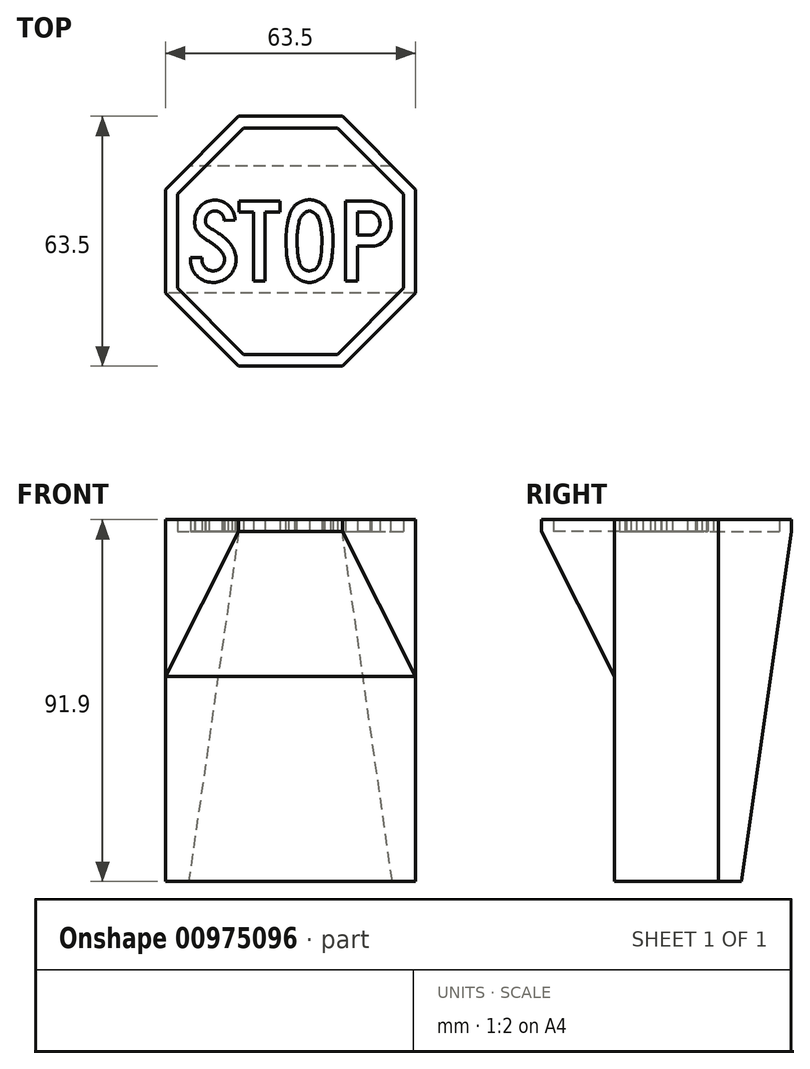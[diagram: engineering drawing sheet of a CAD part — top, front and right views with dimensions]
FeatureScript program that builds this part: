
annotation { "Feature Type Name" : "Feature", "Feature Type Description" : "" }
export const myFeature = defineFeature(function(context is Context, id is Id, definition is map)
    precondition{}
    {
        {
            var Q0;
            Q0=qCreatedBy(makeId("Top.planeOp"),FACE);
            var sketch = newSketch(context, id + "F0", { "sketchPlane" : qUnion([Q0])});
            skCircle(sketch, "E0.cCircle", {"center": v(0, 0) * mm, "radius": 34.37 * mm, "construction": true});
            skLineSegment(sketch, "E0.0", {"start": v(-13.15, 31.75) * mm, "end": v(13.15, 31.75) * mm});
            skLineSegment(sketch, "E0.1", {"start": v(13.15, 31.75) * mm, "end": v(31.75, 13.15) * mm});
            skLineSegment(sketch, "E0.2", {"start": v(31.75, 13.15) * mm, "end": v(31.75, -13.15) * mm});
            skLineSegment(sketch, "E0.3", {"start": v(31.75, -13.15) * mm, "end": v(13.15, -31.75) * mm});
            skLineSegment(sketch, "E0.4", {"start": v(13.15, -31.75) * mm, "end": v(-13.15, -31.75) * mm});
            skLineSegment(sketch, "E0.5", {"start": v(-13.15, -31.75) * mm, "end": v(-31.75, -13.15) * mm});
            skLineSegment(sketch, "E0.6", {"start": v(-31.75, -13.15) * mm, "end": v(-31.75, 13.15) * mm});
            skLineSegment(sketch, "E0.7", {"start": v(-31.75, 13.15) * mm, "end": v(-13.15, 31.75) * mm});
            skSolve(sketch);
        }
        {
            var Q0;
            Q0=qSketchRegion(id+"F0",true);
            extrude(context, id + "F1", {"entities" : qUnion([Q0]), "oppositeDirection" : true, "depth" : 88.9 * mm, "offsetDistance" : 25.4 * mm});
        }
        {
            var Q0;
            Q0=makeQuery(id+"F1.opExtrude","SWEPT_FACE",FACE,{"disambiguationData":[OSD([sQuery(id+"F0.wireOp",EDGE,"E0.6")])]});
            var sketch = newSketch(context, id + "F2", { "sketchPlane" : qUnion([Q0])});
            skLineSegment(sketch, "E1", {"start": v(0, 0) * mm, "end": v(-31.75, 0) * mm});
            skLineSegment(sketch, "E2.MirrorCS", {"start": v(0, 0) * mm, "end": v(31.75, 0) * mm});
            skLineSegment(sketch, "E3", {"start": v(31.75, 0) * mm, "end": v(31.75, -88.9) * mm});
            skLineSegment(sketch, "E4", {"start": v(14.66, -88.9) * mm, "end": v(-31.75, -88.9) * mm});
            skLineSegment(sketch, "E5", {"start": v(-31.75, -88.9) * mm, "end": v(-31.75, 0) * mm});
            skLineSegment(sketch, "E6", {"start": v(14.66, -88.9) * mm, "end": v(8.31, -88.9) * mm});
            skPoint(sketch, "E7.orphan", {"position": v(21.01, -88.9) * mm});
            skLineSegment(sketch, "E8", {"start": v(13.15, -88.9) * mm, "end": v(31.75, -88.9) * mm});
            skLineSegment(sketch, "E9", {"start": v(0, -88.9) * mm, "end": v(-6.35, -88.9) * mm});
            skLineSegment(sketch, "E10", {"start": v(-6.35, -88.9) * mm, "end": v(-12.7, -88.9) * mm});
            skLineSegment(sketch, "E11", {"start": v(-12.7, -88.9) * mm, "end": v(-19.05, -88.9) * mm});
            skLineSegment(sketch, "E12", {"start": v(-13.15, -88.9) * mm, "end": v(31.75, 0) * mm});
            skLineSegment(sketch, "E13", {"start": v(-19.05, -88.9) * mm, "end": v(-31.75, 0) * mm});
            skSolve(sketch);
        }
        {
            var Q0;
            {var subQ0=sQuery(id+"F2.wireOp",EDGE,"E5");Q0=makeQuery(id+"F2.imprint","IMPRINT",FACE,{"disambiguationData":[TD([[makeQuery(id+"F2.imprint","IMPRINT",EDGE,{"derivedFrom":subQ0}),-1.0]])]});}
            var Q1;
            {var subQ0=sQuery(id+"F2.wireOp",EDGE,"jV5SaWTU-9QsE-opv1-VP0P-y0ptpn6lwSnb");var subQ1=sQuery(id+"F0.wireOp",EDGE,"E0.6");var subQ2=makeQuery(id+"F1.opExtrude","SWEPT_EDGE",EDGE,{"disambiguationData":[OSD([sQuery(id+"F0.wireOp",EDGE,"E0.5"),subQ1])]});var subQ3=makeQuery(id+"F2.imprint","INTERSECT",VERTEX,{"derivedFrom":[subQ2,subQ0]});Q1=makeQuery(id+"F2.imprint","IMPRINT",FACE,{"disambiguationData":[TD([[makeQuery(id+"F2.imprint","IMPRINT",EDGE,{"disambiguationData":[TD([[subQ3,-1.0]])],"derivedFrom":subQ0}),1.0]])]});}
            var Q2;
            {var subQ0=sQuery(id+"F2.wireOp",EDGE,"E4");var subQ1=sQuery(id+"F2.wireOp",EDGE,"jV5SaWTU-9QsE-opv1-VP0P-y0ptpn6lwSnb");var subQ2=makeQuery(id+"F2.imprint","INTERSECT",VERTEX,{"derivedFrom":[sQuery(id+"F2.wireOp",EDGE,"heyR2Hmy-5QPG-FOdl-Z93e-mRFAagvmiP7r"),subQ1,subQ0]});Q2=makeQuery(id+"F2.imprint","IMPRINT",FACE,{"disambiguationData":[TD([[makeQuery(id+"F2.imprint","IMPRINT",EDGE,{"disambiguationData":[TD([[subQ2,-1.0]])],"derivedFrom":subQ1}),1.0]])]});}
            var Q3;
            {var subQ4=sQuery(id+"F2.wireOp",EDGE,"JUMX4e05-irpo-ZofT-aYDr-bJa91oU9Ee8P");var subQ6=sQuery(id+"F2.wireOp",EDGE,"AKcFHBRH-ovDV-q2iI-lgTK-DhJX03LWiosI");var subQ7=makeQuery(id+"F2.imprint","INTERSECT",VERTEX,{"derivedFrom":[subQ4,subQ6]});Q3=makeQuery(id+"F2.imprint","IMPRINT",FACE,{"disambiguationData":[TD([[makeQuery(id+"F2.imprint","IMPRINT",EDGE,{"disambiguationData":[TD([[subQ7,1.0]])],"derivedFrom":subQ4}),1.0]])]});}
            var Q4;
            {var subQ0=sQuery(id+"F2.wireOp",EDGE,"E4");var subQ1=makeQuery(id+"F1.opExtrude","SWEPT_EDGE",EDGE,{"disambiguationData":[OSD([sQuery(id+"F0.wireOp",EDGE,"E0.5"),sQuery(id+"F0.wireOp",EDGE,"E0.6")])]});var subQ2=makeQuery(id+"F2.imprint","INTERSECT",VERTEX,{"derivedFrom":[subQ1,subQ0]});Q4=makeQuery(id+"F2.imprint","IMPRINT",FACE,{"disambiguationData":[TD([[makeQuery(id+"F2.imprint","IMPRINT",EDGE,{"disambiguationData":[TD([[subQ2,1.0]])],"derivedFrom":subQ0}),-1.0]])]});}
            var Q5;
            Q5=makeQuery(id+"F1.opExtrude","SWEPT_FACE",FACE,{"disambiguationData":[OSD([sQuery(id+"F0.wireOp",EDGE,"E0.3")])]});
            var Q6;
            {var subQ0=sQuery(id+"F2.wireOp",EDGE,"E3");Q6=makeQuery(id+"F2.imprint","IMPRINT",FACE,{"disambiguationData":[TD([[makeQuery(id+"F2.imprint","IMPRINT",EDGE,{"derivedFrom":subQ0}),-1.0]])]});}
            var Q7;
            {var subQ0=sQuery(id+"F2.wireOp",EDGE,"VHKm9X3M-lhd3-aAJ8-6689-DRtZFMRUWEL7");var subQ1=sQuery(id+"F0.wireOp",EDGE,"E0.6");var subQ2=makeQuery(id+"F1.opExtrude","CAP_EDGE",EDGE,{"disambiguationData":[OSD([subQ1])],"isStart":false});var subQ3=makeQuery(id+"F2.imprint","INTERSECT",VERTEX,{"derivedFrom":[subQ2,sQuery(id+"F2.wireOp",EDGE,"E6"),subQ0]});Q7=makeQuery(id+"F2.imprint","IMPRINT",FACE,{"disambiguationData":[TD([[makeQuery(id+"F2.imprint","IMPRINT",EDGE,{"disambiguationData":[TD([[subQ3,-1.0]])],"derivedFrom":subQ0}),-1.0]])]});}
            var Q8;
            {var subQ4=sQuery(id+"F2.wireOp",EDGE,"E6");Q8=makeQuery(id+"F2.imprint","IMPRINT",FACE,{"disambiguationData":[TD([[makeQuery(id+"F2.imprint","IMPRINT",EDGE,{"derivedFrom":subQ4}),-1.0]])]});}
            var Q9;
            Q9=makeQuery(id+"F1.opExtrude","SWEPT_FACE",FACE,{"disambiguationData":[OSD([sQuery(id+"F0.wireOp",EDGE,"E0.2")])]});
            extrude(context, id + "F3", {"entities" : qUnion([Q0, Q1, Q2, Q3, Q4, Q5, Q6, Q7, Q8]), "operationType" : NewBodyOperationType.REMOVE, "endBound" : BoundingType.UP_TO_SURFACE, "oppositeDirection" : true, "depth" : 25.4 * mm, "endBoundEntityFace" : qUnion([Q9]), "offsetDistance" : 25.4 * mm});
        }
        {
            var Q0;
            Q0=makeQuery(id+"F1.opExtrude","CAP_FACE",FACE,{"disambiguationData":[OSD([sQuery(id+"F0.wireOp",EDGE,"E0.0"),sQuery(id+"F0.wireOp",EDGE,"E0.1"),sQuery(id+"F0.wireOp",EDGE,"E0.2"),sQuery(id+"F0.wireOp",EDGE,"E0.3"),sQuery(id+"F0.wireOp",EDGE,"E0.4"),sQuery(id+"F0.wireOp",EDGE,"E0.5"),sQuery(id+"F0.wireOp",EDGE,"E0.6"),sQuery(id+"F0.wireOp",EDGE,"E0.7")])],"isStart":true});
            var sketch = newSketch(context, id + "F4", { "sketchPlane" : qUnion([Q0])});
            skLineSegment(sketch, "E14.0", {"start": v(-28.75, 11.9) * mm, "end": v(-11.9, 28.75) * mm});
            skLineSegment(sketch, "E14.1", {"start": v(-28.75, -11.9) * mm, "end": v(-28.75, 11.9) * mm});
            skLineSegment(sketch, "E14.2", {"start": v(-11.9, 28.75) * mm, "end": v(11.9, 28.75) * mm});
            skLineSegment(sketch, "E14.3", {"start": v(-11.9, -28.75) * mm, "end": v(-28.75, -11.9) * mm});
            skLineSegment(sketch, "E14.4", {"start": v(11.9, 28.75) * mm, "end": v(28.75, 11.9) * mm});
            skLineSegment(sketch, "E14.5", {"start": v(28.75, 11.9) * mm, "end": v(28.75, -11.9) * mm});
            skLineSegment(sketch, "E14.6", {"start": v(28.75, -11.9) * mm, "end": v(11.9, -28.75) * mm});
            skLineSegment(sketch, "E14.7", {"start": v(11.9, -28.75) * mm, "end": v(-11.9, -28.75) * mm});
            skLineSegment(sketch, "E15.bottom", {"start": v(28.75, -11.9) * mm, "end": v(-28.75, -11.9) * mm});
            skLineSegment(sketch, "E15.top", {"start": v(28.75, 11.9) * mm, "end": v(-28.75, 11.9) * mm});
            skLineSegment(sketch, "E15.left", {"start": v(28.75, -11.9) * mm, "end": v(28.75, 11.9) * mm});
            skPoint(sketch, "E15.middle", {"position": v(0, 0) * mm});
            skLineSegment(sketch, "E16.bottom", {"start": v(33.9, 33.9) * mm, "end": v(-33.9, 33.9) * mm});
            skLineSegment(sketch, "E16.top", {"start": v(33.9, -33.9) * mm, "end": v(-33.9, -33.9) * mm});
            skLineSegment(sketch, "E16.left", {"start": v(33.9, 33.9) * mm, "end": v(33.9, -33.9) * mm});
            skLineSegment(sketch, "E16.right", {"start": v(-33.9, 33.9) * mm, "end": v(-33.9, -33.9) * mm});
            skLineSegment(sketch, "E17", {"start": v(-28.75, -10.78) * mm, "end": v(28.75, -10.78) * mm});
            skLineSegment(sketch, "E18.MirrorCS", {"start": v(-28.75, 10.78) * mm, "end": v(28.75, 10.78) * mm});
            skPoint(sketch, "E19", {"position": v(-22.45, -4.1) * mm});
            skPoint(sketch, "E20", {"position": v(-25.43, -4.1) * mm});
            skPoint(sketch, "E21", {"position": v(-16.83, -4.1) * mm});
            skPoint(sketch, "E22", {"position": v(-20.76, 0) * mm});
            skPoint(sketch, "E23", {"position": v(-20.76, -7.34) * mm});
            skArc(sketch, "E24", {"start": v(-22.45, -4.1) * mm, "mid": v(-18.95, -7.48) * mm, "end": v(-17.44, -2.86) * mm});
            skFitSpline(sketch, "E25", {"points": [v(-20.76, 0) * mm, v(-17.8, -2.36) * mm, v(-16.83, -4.1) * mm], "startDerivative": vector(5.92, -4.06) * mm, "endDerivative": vector(1.7, -4.16) * mm});
            skLineSegment(sketch, "E26", {"start": v(-22.45, -4.1) * mm, "end": v(-25.43, -4.1) * mm});
            skArc(sketch, "E27", {"start": v(-25.43, -4.1) * mm, "mid": v(-18.16, -10.32) * mm, "end": v(-14.9, -1.33) * mm});
            skFitSpline(sketch, "E28", {"points": [v(-15.87, 0) * mm, v(-14.9, -1.33) * mm], "startDerivative": vector(1.2, -1.18) * mm, "endDerivative": vector(0.57, -1.44) * mm});
            skPoint(sketch, "E29.trimOffspring.end.orphan", {"position": v(-27.32, 0) * mm});
            skPoint(sketch, "E30", {"position": v(-16.86, 5.28) * mm});
            skPoint(sketch, "E31", {"position": v(-14.12, 5.32) * mm});
            skPoint(sketch, "E32", {"position": v(-21.58, 5.28) * mm});
            skPoint(sketch, "E33", {"position": v(-19.24, 7.66) * mm});
            skArc(sketch, "E34", {"start": v(-16.86, 5.28) * mm, "mid": v(-19.22, 7.66) * mm, "end": v(-21.58, 5.28) * mm});
            skFitSpline(sketch, "E35", {"points": [v(-21.58, 5.28) * mm, v(-21.4, 4.17) * mm, v(-18.58, 2.21) * mm, v(-15.87, 0) * mm], "startDerivative": vector(-0.47, -5.02) * mm, "endDerivative": vector(6.25, -5.82) * mm});
            skArc(sketch, "E36", {"start": v(-14.12, 5.32) * mm, "mid": v(-19.23, 10.4) * mm, "end": v(-24.32, 5.3) * mm});
            skFitSpline(sketch, "E37", {"points": [v(-24.32, 5.3) * mm, v(-24.22, 3.6) * mm, v(-22.95, 1.57) * mm, v(-20.76, 0) * mm], "startDerivative": vector(-0.33, -5.74) * mm, "endDerivative": vector(6.39, -3.84) * mm});
            skLineSegment(sketch, "E38", {"start": v(-16.86, 5.28) * mm, "end": v(-14.12, 5.32) * mm});
            skPoint(sketch, "E39.start.orphan", {"position": v(-12.29, 0) * mm});
            skLineSegment(sketch, "E40.bottom", {"start": v(-9.37, -10.14) * mm, "end": v(-6.43, -10.14) * mm});
            skLineSegment(sketch, "E40.top", {"start": v(-9.37, 10.14) * mm, "end": v(-6.43, 10.14) * mm});
            skLineSegment(sketch, "E40.left", {"start": v(-9.37, -10.14) * mm, "end": v(-9.37, 7.43) * mm});
            skLineSegment(sketch, "E40.right", {"start": v(-6.43, -10.14) * mm, "end": v(-6.43, 7.43) * mm});
            skLineSegment(sketch, "E41.top", {"start": v(-2.65, 7.43) * mm, "end": v(-6.43, 7.43) * mm});
            skLineSegment(sketch, "E41.left", {"start": v(-2.65, 10.14) * mm, "end": v(-2.65, 7.43) * mm});
            skLineSegment(sketch, "E41.right", {"start": v(-13.03, 10.14) * mm, "end": v(-13.03, 7.43) * mm});
            skLineSegment(sketch, "E42", {"start": v(-9.37, 10.14) * mm, "end": v(-13.03, 10.14) * mm});
            skLineSegment(sketch, "E43", {"start": v(-6.43, 10.14) * mm, "end": v(-2.65, 10.14) * mm});
            skPoint(sketch, "E44.orphan", {"position": v(-13.03, 10.32) * mm});
            skLineSegment(sketch, "E45.trimOffspring", {"start": v(-9.37, 7.43) * mm, "end": v(-13.03, 7.43) * mm});
            skLineSegment(sketch, "E46", {"start": v(13.96, 10.14) * mm, "end": v(13.96, -10.14) * mm});
            skLineSegment(sketch, "E47", {"start": v(13.96, -10.14) * mm, "end": v(16.98, -10.14) * mm});
            skLineSegment(sketch, "E48", {"start": v(16.98, -10.14) * mm, "end": v(16.98, -1.27) * mm});
            skLineSegment(sketch, "E49", {"start": v(13.96, 10.14) * mm, "end": v(20.6, 10.14) * mm});
            skLineSegment(sketch, "E50", {"start": v(16.98, 1.51) * mm, "end": v(16.98, 7.43) * mm});
            skLineSegment(sketch, "E51", {"start": v(16.98, 7.43) * mm, "end": v(20.22, 7.43) * mm});
            skLineSegment(sketch, "E52", {"start": v(20.22, 1.51) * mm, "end": v(16.98, 1.51) * mm});
            skFitSpline(sketch, "E53", {"points": [v(20.22, 7.43) * mm, v(22.37, 5.9) * mm, v(22.43, 3.23) * mm, v(20.22, 1.51) * mm], "startDerivative": vector(8.54, -0.14) * mm, "endDerivative": vector(-8.25, 0.77) * mm});
            skLineSegment(sketch, "E54", {"start": v(16.98, -1.27) * mm, "end": v(20.6, -1.27) * mm});
            skPoint(sketch, "E55", {"position": v(4.8, 10.54) * mm});
            skLineSegment(sketch, "E56", {"start": v(0, 0) * mm, "end": v(4.8, 0) * mm});
            skPoint(sketch, "E57.MirrorP", {"position": v(4.8, -10.54) * mm});
            skFitSpline(sketch, "E58", {"points": [v(4.8, 10.54) * mm, v(1.72, 9.54) * mm, v(-0.36, 6.48) * mm, v(-0.9, -4.8) * mm, v(1.95, -9.7) * mm, v(4.8, -10.54) * mm, v(8.77, -8.69) * mm, v(10.48, -4.31) * mm, v(10.4, 4.6) * mm, v(8.01, 9.55) * mm, v(4.8, 10.54) * mm]});
            skLineSegment(sketch, "E59", {"start": v(4.8, 0) * mm, "end": v(4.8, 2.13) * mm});
            skFitSpline(sketch, "E60.MirrorCS", {"points": [v(4.8, 10.54) * mm, v(7.9, 9.54) * mm, v(9.97, 6.48) * mm, v(10.5, -4.8) * mm, v(7.66, -9.7) * mm, v(4.8, -10.54) * mm, v(0.84, -8.69) * mm, v(-0.87, -4.31) * mm, v(-0.78, 4.6) * mm, v(1.6, 9.55) * mm, v(4.8, 10.54) * mm]});
            skPoint(sketch, "E61", {"position": v(4.8, 7.79) * mm});
            skPoint(sketch, "E62", {"position": v(4.8, -7.62) * mm});
            skFitSpline(sketch, "E63", {"points": [v(4.8, 7.79) * mm, v(2.55, 5.95) * mm, v(1.84, -3.12) * mm, v(3.07, -6.9) * mm, v(4.8, -7.62) * mm], "startDerivative": vector(-12.15, -5.2) * mm, "endDerivative": vector(11.19, -2.47) * mm});
            skFitSpline(sketch, "E64.MirrorCS", {"points": [v(4.8, 7.79) * mm, v(7.07, 5.95) * mm, v(7.77, -3.12) * mm, v(6.54, -6.9) * mm, v(4.8, -7.62) * mm], "startDerivative": vector(12.15, -5.2) * mm, "endDerivative": vector(-11.19, -2.47) * mm});
            skFitSpline(sketch, "E65", {"points": [v(20.6, 10.14) * mm, v(23.97, 8.83) * mm, v(25.32, 6.13) * mm, v(25.42, 2.7) * mm, v(23.87, 0) * mm, v(21.38, -1.27) * mm, v(20.6, -1.27) * mm], "startDerivative": vector(19.7, -4.63) * mm, "endDerivative": vector(-7.28, 1.07) * mm});
            skLineSegment(sketch, "E66", {"start": v(-13.15, 31.75) * mm, "end": v(13.15, 31.75) * mm});
            skLineSegment(sketch, "E67", {"start": v(13.15, 31.75) * mm, "end": v(31.75, 13.15) * mm});
            skLineSegment(sketch, "E68", {"start": v(31.75, 13.15) * mm, "end": v(31.75, -13.15) * mm});
            skLineSegment(sketch, "E69", {"start": v(31.75, -13.15) * mm, "end": v(13.15, -31.75) * mm});
            skLineSegment(sketch, "E70", {"start": v(13.15, -31.75) * mm, "end": v(-13.15, -31.75) * mm});
            skLineSegment(sketch, "E71", {"start": v(-13.15, -31.75) * mm, "end": v(-31.75, -13.15) * mm});
            skLineSegment(sketch, "E72", {"start": v(-31.75, -13.15) * mm, "end": v(-31.75, 13.15) * mm});
            skLineSegment(sketch, "E73", {"start": v(-31.75, 13.15) * mm, "end": v(-13.15, 31.75) * mm});
            skSolve(sketch);
        }
        {
            var Q0;
            {var subQ12=sQuery(id+"F4.wireOp",EDGE,"E14.0");Q0=makeQuery(id+"F4.imprint","IMPRINT",FACE,{"disambiguationData":[TD([[makeQuery(id+"F4.imprint","IMPRINT",EDGE,{"derivedFrom":subQ12}),1.0]])]});}
            var Q1;
            Q1=makeQuery(id+"F4.imprint","IMPRINT",FACE,{"disambiguationData":[TD([[makeQuery(id+"F4.imprint","IMPRINT",EDGE,{"derivedFrom":sQuery(id+"F4.wireOp",EDGE,"E24")}),-1.0]])]});
            var Q2;
            Q2=makeQuery(id+"F4.imprint","IMPRINT",FACE,{"disambiguationData":[TD([[makeQuery(id+"F4.imprint","IMPRINT",EDGE,{"derivedFrom":sQuery(id+"F4.wireOp",EDGE,"E40.bottom")}),1.0]])]});
            var Q3;
            Q3=makeQuery(id+"F4.imprint","IMPRINT",FACE,{"disambiguationData":[TD([[makeQuery(id+"F4.imprint","IMPRINT",EDGE,{"derivedFrom":sQuery(id+"F4.wireOp",EDGE,"E58")}),1.0]])]});
            var Q4;
            Q4=makeQuery(id+"F4.imprint","IMPRINT",FACE,{"disambiguationData":[TD([[makeQuery(id+"F4.imprint","IMPRINT",EDGE,{"derivedFrom":sQuery(id+"F4.wireOp",EDGE,"E46")}),1.0]])]});
            extrude(context, id + "F5", {"entities" : qUnion([Q0, Q1, Q2, Q3, Q4]), "operationType" : NewBodyOperationType.ADD, "depth" : 3 * mm, "offsetDistance" : 25.4 * mm});
        }
    });
